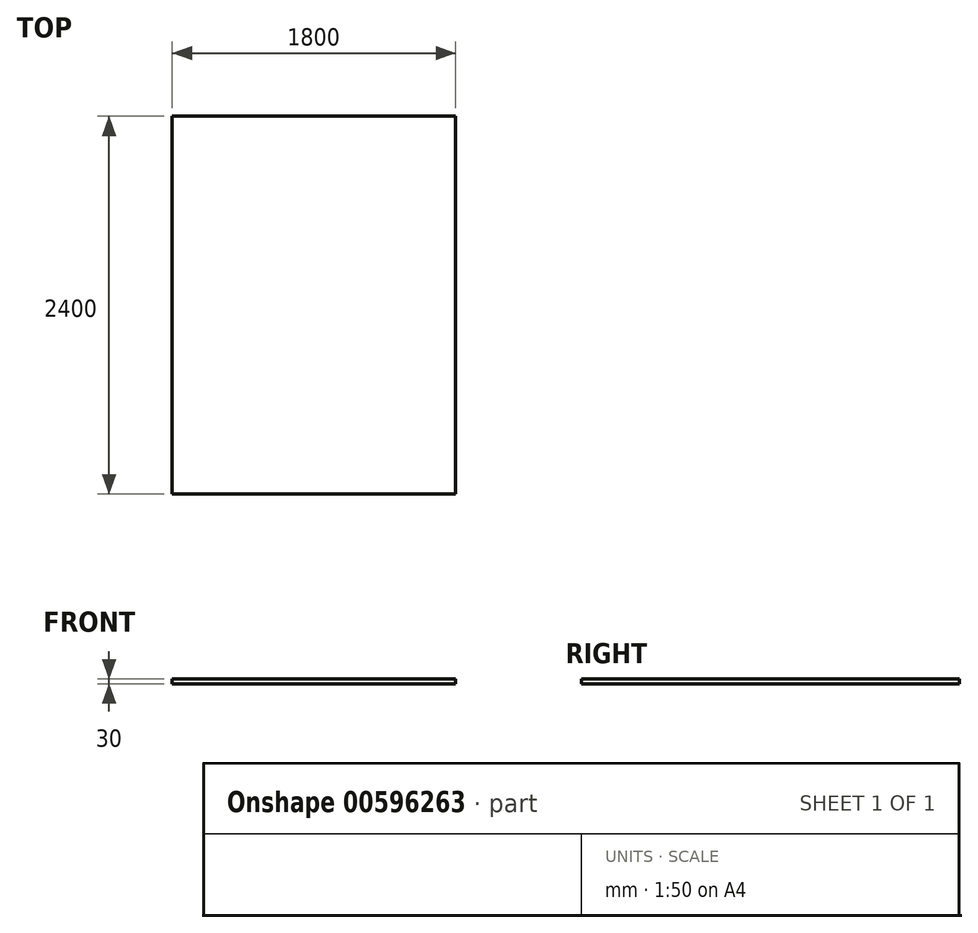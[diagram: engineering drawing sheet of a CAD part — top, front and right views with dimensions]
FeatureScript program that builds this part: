
annotation { "Feature Type Name" : "Feature", "Feature Type Description" : "" }
export const myFeature = defineFeature(function(context is Context, id is Id, definition is map)
    precondition{}
    {
        {
            var Q0;
            Q0=qCreatedBy(makeId("Top.planeOp"),FACE);
            var sketch = newSketch(context, id + "F0", { "sketchPlane" : qUnion([Q0])});
            skLineSegment(sketch, "E0.bottom", {"start": v(-900, 1200) * mm, "end": v(900, 1200) * mm});
            skLineSegment(sketch, "E0.top", {"start": v(-900, -1200) * mm, "end": v(900, -1200) * mm});
            skLineSegment(sketch, "E0.left", {"start": v(-900, 1200) * mm, "end": v(-900, -1200) * mm});
            skLineSegment(sketch, "E0.right", {"start": v(900, 1200) * mm, "end": v(900, -1200) * mm});
            skSolve(sketch);
        }
        {
            var Q0;
            Q0=makeQuery(id+"F0.imprint","IMPRINT",FACE,{"disambiguationData":[TD([[makeQuery(id+"F0.imprint","IMPRINT",EDGE,{"derivedFrom":sQuery(id+"F0.wireOp",EDGE,"E0.bottom")}),-1.0]])]});
            extrude(context, id + "F1", {"entities" : qUnion([Q0]), "depth" : 30 * mm, "offsetDistance" : 25 * mm});
        }
    });
